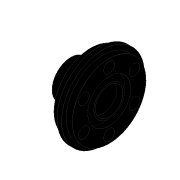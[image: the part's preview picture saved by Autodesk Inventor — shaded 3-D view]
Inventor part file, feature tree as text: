
AUTODESK INVENTOR PART (.ipt)
format: ipt  version: 2020 (Build 240168000, 168)  size: 404,480 bytes
history: native  units: in
note: dims shown in document units (in); Inventor stores cm internally (conversion verified against a paired STEP export)
features: extrude x8, sketch x8, projected_geometry x2, chamfer x1
ambient origin geometry x8: Origin, YZ Plane, XZ Plane, XY Plane, X Axis, Y Axis, Z Axis, Center Point
bodies: Solid1 (feature_tree)
feature tree (19):
  extrude  "Extrusion1"  Depth=0.3937in
  extrude  "Extrusion2"  Depth=0.1969in
  extrude  "Extrusion3"  Depth=0.7874in
  extrude  "Extrusion4"  Depth=0.0394in TaperAngle=0.0deg
  extrude  "Extrusion5"  Depth=0.1181in TaperAngle=0.0deg
  chamfer  "Chamfer1"  Distance=0.1181in
  extrude  "Extrusion6"  Depth=0.9843in
  extrude  "Extrusion7"  Depth=0.2756in
  extrude  "Extrusion8"  Depth=0.1969in TaperAngle=360.0deg
  sketch  "Sketch1"  dims[d0=1.8898in d1=0.3937in]
  sketch  "Sketch2"  dims[d2=0.1969in d3=0.2756in]
  projected_geometry  "Projected Loop1"
  sketch  "Sketch3"  dims[d4=2.3622in d6=360.0deg d8=0.7874in]
  projected_geometry  "Projected Loop2"
  sketch  "Sketch4"  dims[d9=0.0394in d10=0.1575in d11=0.0in]
  sketch  "Sketch5"  dims[d12=0.1181in d13=0.1181in d14=0.0in d15=0.1181in d16=0.0in]
  sketch  "Sketch6"  dims[d17=0.0787in d18=0.0in d19=0.9843in]
  sketch  "Sketch7"  dims[d20=0.2756in d21=0.0in d22=0.2756in d23=0.125in d24=0.0137in]
  sketch  "Sketch8"  dims[d25=0.0157in d26=2.3622in d28=360.0deg d30=0.2756in d31=0.0in d32=0.0394in d33=0.0in d35=0.0394in d36=0.0866in d37=0.0827in d38=0.0827in d39=0.0827in d40=5.9055in d42=360.0deg d44=0.1969in d45=0.0in]
